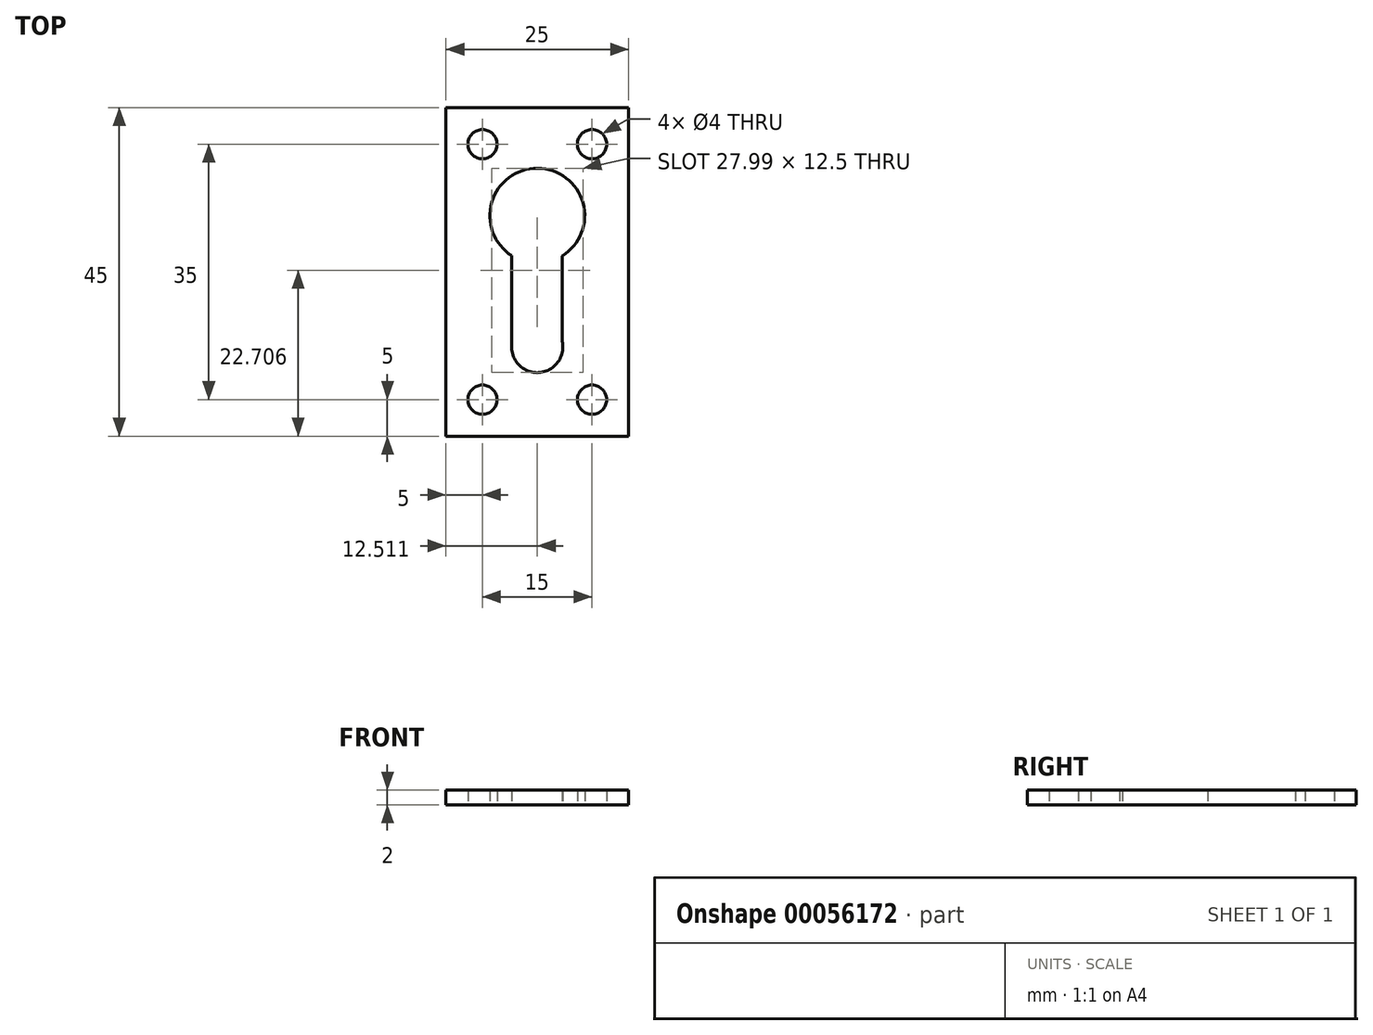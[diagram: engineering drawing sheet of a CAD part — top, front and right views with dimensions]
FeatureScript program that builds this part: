
annotation { "Feature Type Name" : "Feature", "Feature Type Description" : "" }
export const myFeature = defineFeature(function(context is Context, id is Id, definition is map)
    precondition{}
    {
        {
            var Q0;
            Q0=qCreatedBy(makeId("Top.planeOp"),FACE);
            var sketch = newSketch(context, id + "F0", { "sketchPlane" : qUnion([Q0])});
            skLineSegment(sketch, "E0.bottom", {"start": v(-12.5, 22.5) * mm, "end": v(12.5, 22.5) * mm});
            skLineSegment(sketch, "E0.top", {"start": v(-12.5, -22.5) * mm, "end": v(12.5, -22.5) * mm});
            skLineSegment(sketch, "E0.left", {"start": v(-12.5, 22.5) * mm, "end": v(-12.5, -22.5) * mm});
            skLineSegment(sketch, "E0.right", {"start": v(12.5, 22.5) * mm, "end": v(12.5, -22.5) * mm});
            skPoint(sketch, "E1", {"position": v(0, 22.5) * mm});
            skPoint(sketch, "E2", {"position": v(12.5, 0) * mm});
            skArc(sketch, "E3", {"start": v(3.4, 2.17) * mm, "mid": v(0.04, 14.2) * mm, "end": v(-3.48, 2.21) * mm});
            skArc(sketch, "E4", {"start": v(-3.48, -9.9) * mm, "mid": v(0.2, -13.8) * mm, "end": v(3.4, -9.5) * mm});
            skLineSegment(sketch, "E5", {"start": v(-3.48, -9.9) * mm, "end": v(-3.48, 2.21) * mm});
            skLineSegment(sketch, "E6", {"start": v(3.4, -9.5) * mm, "end": v(3.4, 2.17) * mm});
            skCircle(sketch, "E7", {"center": v(-7.5, 17.5) * mm, "radius": 2 * mm});
            skCircle(sketch, "E8", {"center": v(-7.5, 17.5) * mm, "radius": 4 * mm, "construction": true});
            skLineSegment(sketch, "E9", {"start": v(0, 22.5) * mm, "end": v(0, -22.5) * mm, "construction": true});
            skCircle(sketch, "E10.MirrorC", {"center": v(7.5, 17.5) * mm, "radius": 4 * mm, "construction": true});
            skCircle(sketch, "E11.MirrorC", {"center": v(7.5, 17.5) * mm, "radius": 2 * mm});
            skLineSegment(sketch, "E12", {"start": v(0, 0) * mm, "end": v(12.5, 0) * mm, "construction": true});
            skCircle(sketch, "E13.MirrorC", {"center": v(7.5, -17.5) * mm, "radius": 2 * mm});
            skCircle(sketch, "E14.MirrorC", {"center": v(7.5, -17.5) * mm, "radius": 4 * mm, "construction": true});
            skCircle(sketch, "E15.MirrorC", {"center": v(-7.5, -17.5) * mm, "radius": 4 * mm, "construction": true});
            skCircle(sketch, "E16.MirrorC", {"center": v(-7.5, -17.5) * mm, "radius": 2 * mm});
            skSolve(sketch);
        }
        {
            var Q0;
            Q0 = qSketchRegion(id + "F0", true);
            extrude(context, id + "F1", {"entities" : qUnion([Q0]), "depth" : 2 * mm});
        }
    });
